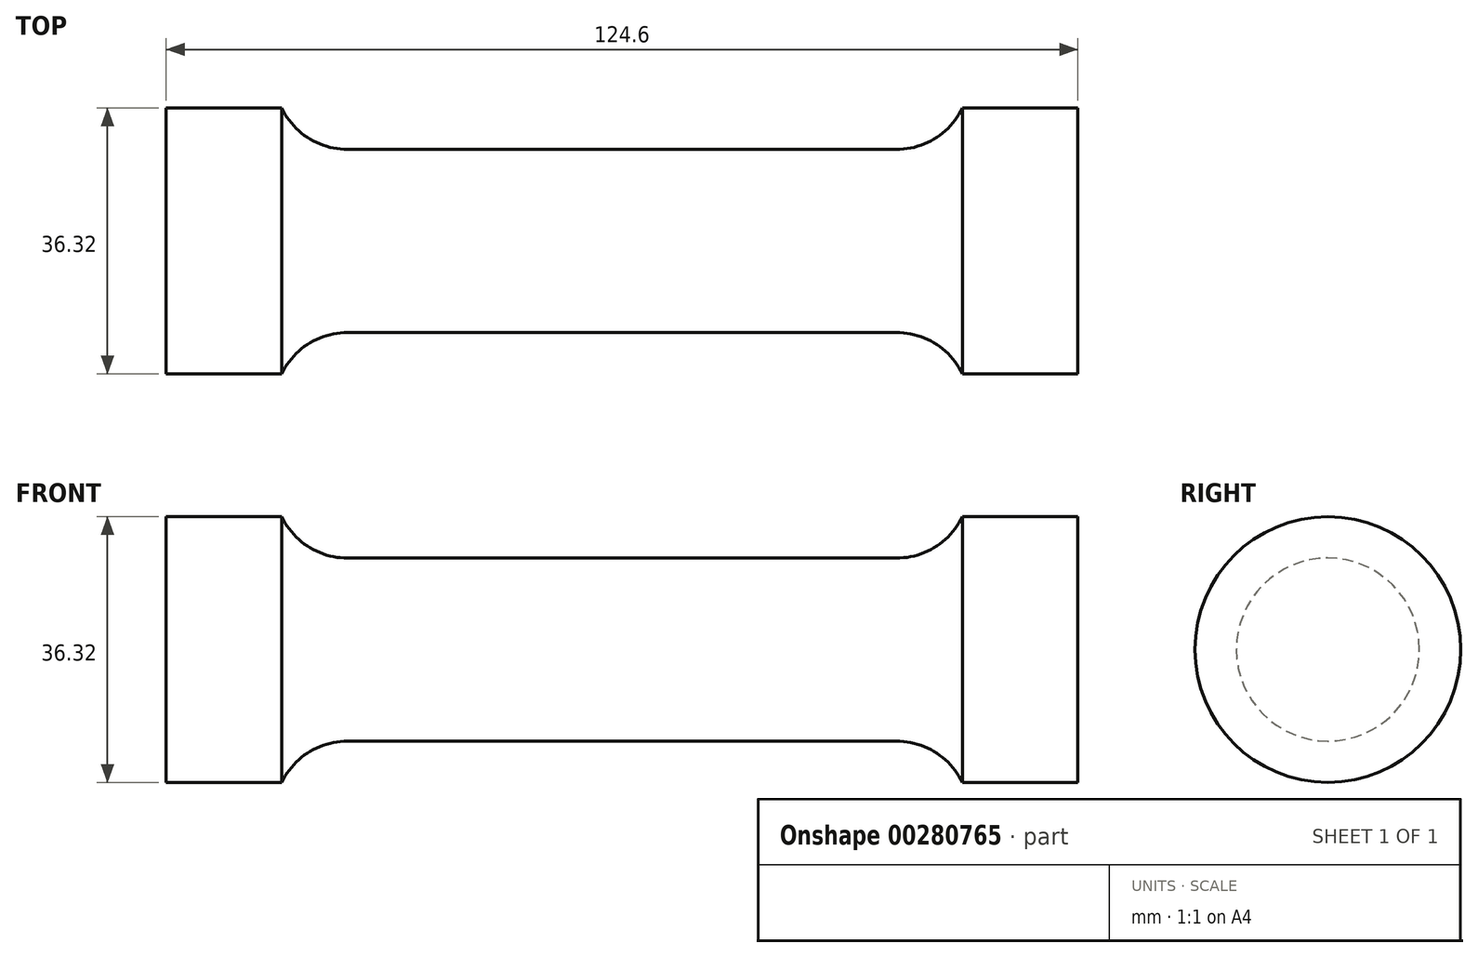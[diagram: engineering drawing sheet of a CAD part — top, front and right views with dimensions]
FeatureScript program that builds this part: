
annotation { "Feature Type Name" : "Feature", "Feature Type Description" : "" }
export const myFeature = defineFeature(function(context is Context, id is Id, definition is map)
    precondition{}
    {
        {
            var Q0;
            Q0=qCreatedBy(makeId("Front.planeOp"),FACE);
            var sketch = newSketch(context, id + "F0", { "sketchPlane" : qUnion([Q0])});
            skLineSegment(sketch, "E0", {"start": v(0, 12.5) * mm, "end": v(37.5, 12.5) * mm});
            skArc(sketch, "E1", {"start": v(37.5, 12.5) * mm, "mid": v(42.82, 14.03) * mm, "end": v(46.5, 18.16) * mm});
            skLineSegment(sketch, "E2", {"start": v(46.5, 18.16) * mm, "end": v(62.3, 18.16) * mm});
            skLineSegment(sketch, "E3", {"start": v(62.3, 18.16) * mm, "end": v(62.3, 0) * mm});
            skLineSegment(sketch, "E4.MirrorCS", {"start": v(0, 12.5) * mm, "end": v(-37.5, 12.5) * mm});
            skLineSegment(sketch, "E5.MirrorCS", {"start": v(-62.3, 18.16) * mm, "end": v(-62.3, 0) * mm});
            skLineSegment(sketch, "E6.MirrorCS", {"start": v(-46.5, 18.16) * mm, "end": v(-62.3, 18.16) * mm});
            skArc(sketch, "E7.MirrorCS", {"start": v(-37.5, 12.5) * mm, "mid": v(-42.82, 14.03) * mm, "end": v(-46.5, 18.16) * mm});
            skLineSegment(sketch, "E8", {"start": v(-62.3, 0) * mm, "end": v(62.3, 0) * mm});
            skSolve(sketch);
        }
        {
            var Q0;
            Q0 = qSketchRegion(id + "F0", true);
            var Q1;
            Q1=sQuery(id+"F0.wireOp",EDGE,"E8");
            revolve(context, id + "F1", {"entities" : qUnion([Q0]), "axis" : qUnion([Q1]), "revolveType" : RevolveType.FULL});
        }
    });
